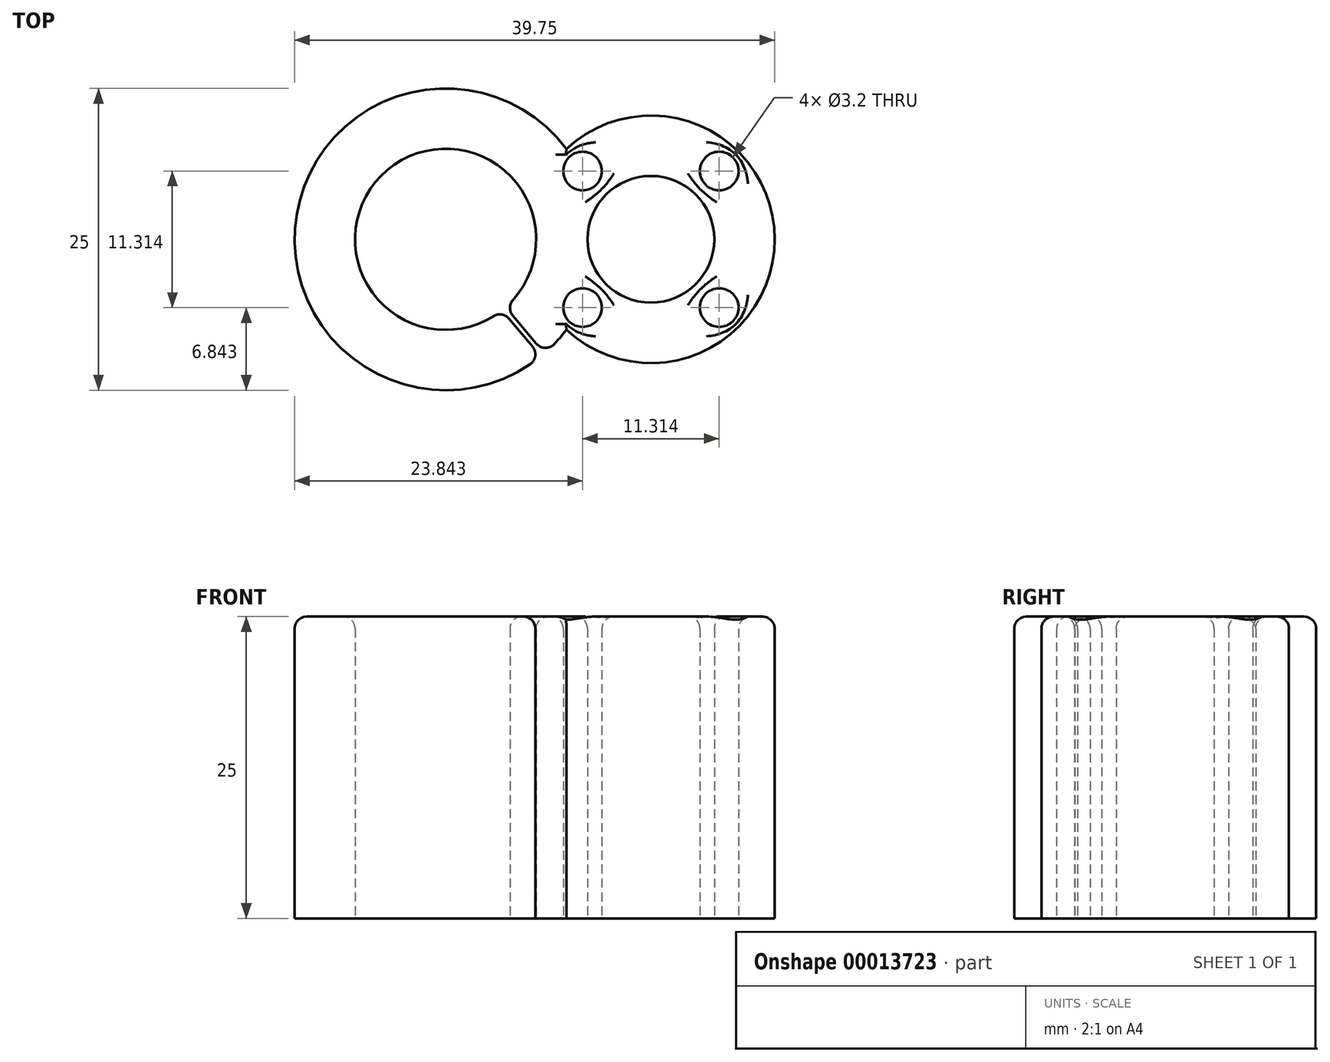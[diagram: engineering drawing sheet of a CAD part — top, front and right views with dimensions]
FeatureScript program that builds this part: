
annotation { "Feature Type Name" : "Feature", "Feature Type Description" : "" }
export const myFeature = defineFeature(function(context is Context, id is Id, definition is map)
    precondition{}
    {
        {
            var Q0;
            Q0=qCreatedBy(makeId("Top.planeOp"),FACE);
            var sketch = newSketch(context, id + "F0", { "sketchPlane" : qUnion([Q0])});
            skCircle(sketch, "E0", {"center": v(0, 0) * mm, "radius": 7.5 * mm});
            skCircle(sketch, "E1", {"center": v(17, 0) * mm, "radius": 5.25 * mm});
            skArc(sketch, "E2.0", {"start": v(10, 7.5) * mm, "mid": v(-12.5, 0) * mm, "end": v(10, -7.5) * mm});
            skArc(sketch, "E3.0", {"start": v(10, -7.5) * mm, "mid": v(27.25, 0) * mm, "end": v(10, 7.5) * mm});
            skCircle(sketch, "E4", {"center": v(17, 0) * mm, "radius": 8 * mm, "construction": true});
            skCircle(sketch, "E5", {"center": v(22.66, 5.66) * mm, "radius": 1.6 * mm});
            skCircle(sketch, "E6", {"center": v(11.34, 5.66) * mm, "radius": 1.6 * mm});
            skCircle(sketch, "E7", {"center": v(22.66, -5.66) * mm, "radius": 1.6 * mm});
            skCircle(sketch, "E8", {"center": v(11.34, -5.66) * mm, "radius": 1.6 * mm});
            skLineSegment(sketch, "E9", {"start": v(0, 0) * mm, "end": v(17, 0) * mm, "construction": true});
            skLineSegment(sketch, "E10", {"start": v(11.34, 5.66) * mm, "end": v(17, 0) * mm, "construction": true});
            skLineSegment(sketch, "E11", {"start": v(0, 0) * mm, "end": v(8.03, -9.58) * mm, "construction": true});
            skLineSegment(sketch, "E12", {"start": v(4.97, -5.61) * mm, "end": v(8.19, -9.45) * mm});
            skLineSegment(sketch, "E13", {"start": v(4.67, -5.87) * mm, "end": v(7.88, -9.7) * mm});
            skSolve(sketch);
        }
        {
            var Q0;
            Q0=makeQuery(id+"F0.imprint","IMPRINT",FACE,{"disambiguationData":[TD([[makeQuery(id+"F0.imprint","IMPRINT",EDGE,{"derivedFrom":sQuery(id+"F0.wireOp",EDGE,"E1")}),-1.0]])]});
            extrude(context, id + "F1", {"entities" : qUnion([Q0]), "depth" : 25 * mm});
        }
        {
            var Q0;
            Q0=makeQuery(id+"F1.opExtrude","SWEPT_EDGE",EDGE,{"disambiguationData":[OSD([sQuery(id+"F0.wireOp",EDGE,"E0"),sQuery(id+"F0.wireOp",EDGE,"E13")])]});
            var Q1;
            Q1=makeQuery(id+"F1.opExtrude","SWEPT_EDGE",EDGE,{"disambiguationData":[OSD([sQuery(id+"F0.wireOp",EDGE,"E0"),sQuery(id+"F0.wireOp",EDGE,"E12")])]});
            var Q2;
            Q2=makeQuery(id+"F1.opExtrude","SWEPT_EDGE",EDGE,{"disambiguationData":[OSD([sQuery(id+"F0.wireOp",EDGE,"E2.0"),sQuery(id+"F0.wireOp",EDGE,"E12")])]});
            var Q3;
            Q3=makeQuery(id+"F1.opExtrude","SWEPT_EDGE",EDGE,{"disambiguationData":[OSD([sQuery(id+"F0.wireOp",EDGE,"E2.0"),sQuery(id+"F0.wireOp",EDGE,"E13")])]});
            fillet(context, id + "F2", {"entities" : qUnion([Q0, Q1, Q2, Q3]), "radius" : 1 * mm, "tangentPropagation" : true, "allowEdgeOverflow" : false});
        }
        {
            var Q0;
            Q0=makeQuery(id+"F1.opExtrude","CAP_EDGE",EDGE,{"disambiguationData":[OSD([sQuery(id+"F0.wireOp",EDGE,"E0")])],"isStart":false});
            var Q1;
            Q1=makeQuery(id+"F1.opExtrude","CAP_EDGE",EDGE,{"disambiguationData":[OSD([sQuery(id+"F0.wireOp",EDGE,"E1")])],"isStart":false});
            var Q2;
            Q2=makeQuery(id+"F1.opExtrude","CAP_FACE",FACE,{"disambiguationData":[OSD([sQuery(id+"F0.wireOp",EDGE,"E0"),sQuery(id+"F0.wireOp",EDGE,"E1"),sQuery(id+"F0.wireOp",EDGE,"E2.0"),sQuery(id+"F0.wireOp",EDGE,"E3.0"),sQuery(id+"F0.wireOp",EDGE,"E5"),sQuery(id+"F0.wireOp",EDGE,"E6"),sQuery(id+"F0.wireOp",EDGE,"E7"),sQuery(id+"F0.wireOp",EDGE,"E8"),sQuery(id+"F0.wireOp",EDGE,"E12"),sQuery(id+"F0.wireOp",EDGE,"E13")])],"isStart":false});
            var Q3;
            Q3=makeQuery(id+"F1.opExtrude","CAP_EDGE",EDGE,{"disambiguationData":[OSD([sQuery(id+"F0.wireOp",EDGE,"E3.0")])],"isStart":false});
            fillet(context, id + "F3", {"entities" : qUnion([Q0, Q1, Q2, Q3]), "radius" : 1 * mm, "tangentPropagation" : true, "allowEdgeOverflow" : false});
        }
    });
